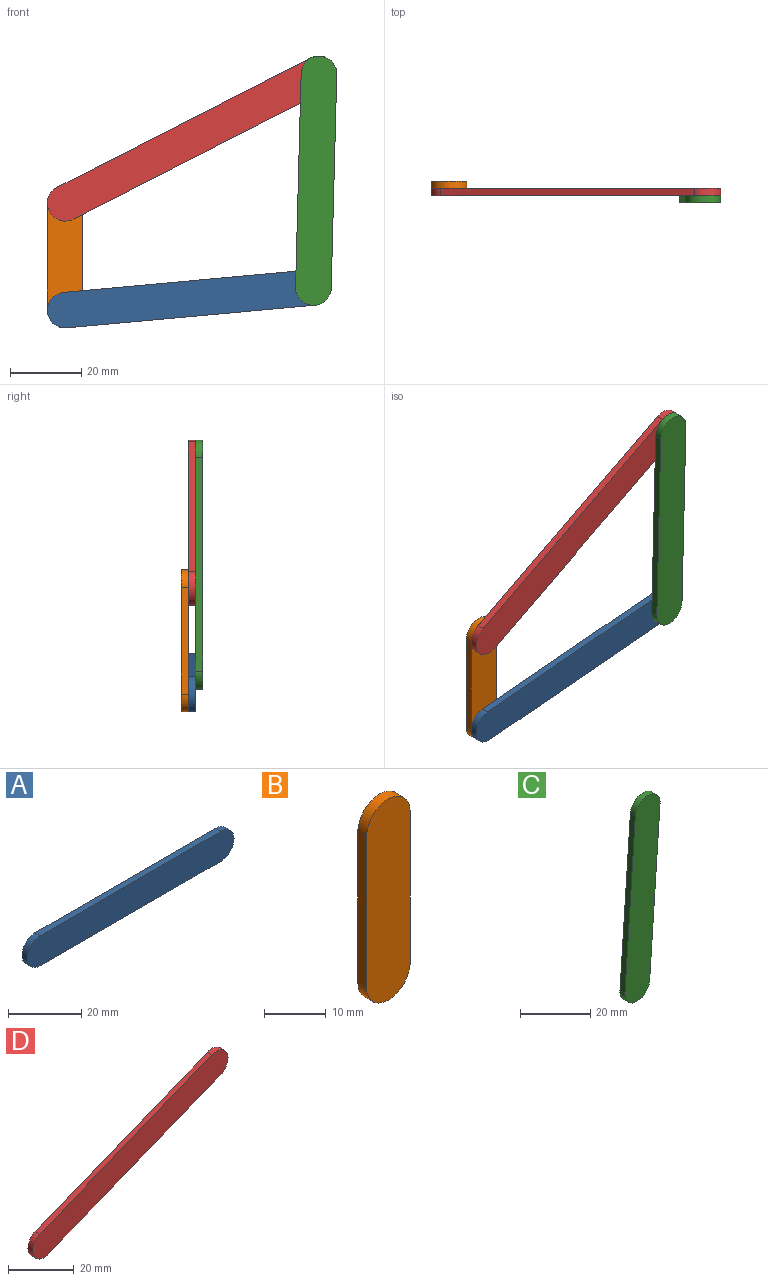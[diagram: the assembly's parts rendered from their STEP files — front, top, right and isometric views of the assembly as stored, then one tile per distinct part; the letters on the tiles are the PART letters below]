
ASSEMBLY  parts=4 mates=4
PART A: 6 faces, bbox 80x2x10 mm
  f0: cylinder r=5mm len=10mm, axis (0,1,0), area 31.4mm2, adj f1,f3,f4,f5
  f1: plane 70x2mm, normal (0,0,1), area 140mm2, adj f0,f2,f4,f5
  f2: cylinder r=5mm len=10mm, axis (0,1,0), area 31.4mm2, adj f1,f3,f4,f5
  f3: plane 70x2mm, normal (0,0,-1), area 140mm2, adj f0,f2,f4,f5
  f4: plane 80x10mm, normal (0,-1,0), area 778.5mm2, adj f0,f1,f2,f3
  f5: plane 80x10mm, normal (0,1,0), area 778.5mm2, adj f0,f1,f2,f3
PART B: 6 faces, bbox 10x2x40 mm
  f0: cylinder r=5mm len=10mm, axis (0,-1,0), area 31.4mm2, adj f1,f3,f4,f5
  f1: plane 30x2mm, normal (-1,0,0), area 60mm2, adj f0,f2,f4,f5
  f2: cylinder r=5mm len=10mm, axis (0,-1,0), area 31.4mm2, adj f1,f3,f4,f5
  f3: plane 30x2mm, normal (1,0,0), area 60mm2, adj f0,f2,f4,f5
  f4: plane 40x10mm, normal (0,1,0), area 378.5mm2, adj f0,f1,f2,f3
  f5: plane 40x10mm, normal (0,-1,0), area 378.5mm2, adj f0,f1,f2,f3
PART C: 6 faces, bbox 14.2x2x69.9 mm
  f0: cylinder r=5mm len=9.99mm, axis (0,1,0), area 31.4mm2, adj f1,f3,f4,f5
  f1: plane 59.85x4.22mm, normal (1,0,-0.07), area 120mm2, adj f0,f2,f4,f5
  f2: cylinder r=5mm len=9.99mm, axis (0,1,0), area 31.4mm2, adj f1,f3,f4,f5
  f3: plane 59.85x4.22mm, normal (-1,0,0.07), area 120mm2, adj f0,f2,f4,f5
  f4: plane 69.85x14.22mm, normal (0,-1,0), area 678.5mm2, adj f0,f1,f2,f3
  f5: plane 69.85x14.22mm, normal (0,1,0), area 678.5mm2, adj f0,f1,f2,f3
PART D: 6 faces, bbox 84.2x2x39.9 mm
  f0: cylinder r=5mm len=9.64mm, axis (0,1,0), area 31.4mm2, adj f1,f3,f4,f5
  f1: plane 74.22x29.85mm, normal (0.37,0,-0.93), area 160mm2, adj f0,f2,f4,f5
  f2: cylinder r=5mm len=9.64mm, axis (0,1,0), area 31.4mm2, adj f1,f3,f4,f5
  f3: plane 74.22x29.85mm, normal (-0.37,0,0.93), area 160mm2, adj f0,f2,f4,f5
  f4: plane 84.22x39.85mm, normal (0,-1,0), area 878.5mm2, adj f0,f1,f2,f3
  f5: plane 84.22x39.85mm, normal (0,1,0), area 878.5mm2, adj f0,f1,f2,f3
PLACE A rot(axis=(0,-1,0),5.2deg) t=(-0.14,0,3.18)mm
PLACE B at identity fixed
PLACE C rot(axis=(0,-1,0),2.5deg) t=(-0.25,0,4.8)mm
PLACE D rot(axis=(0,-1,0),5.1deg) t=(2.53,0,3.23)mm
MATE revolute B.f0 <-> A.f2  axis (0,-1,0) through (-35,0,0)mm
MATE revolute A.f0 <-> C.f0  axis (0,-1,0) through (34.71,-2,6.36)mm
MATE revolute B.f2 <-> D.f0  axis (0,-1,0) through (-35,0,30)mm
MATE revolute C.f2 <-> D.f2  axis (0,1,0) through (36.27,-2,66.34)mm
